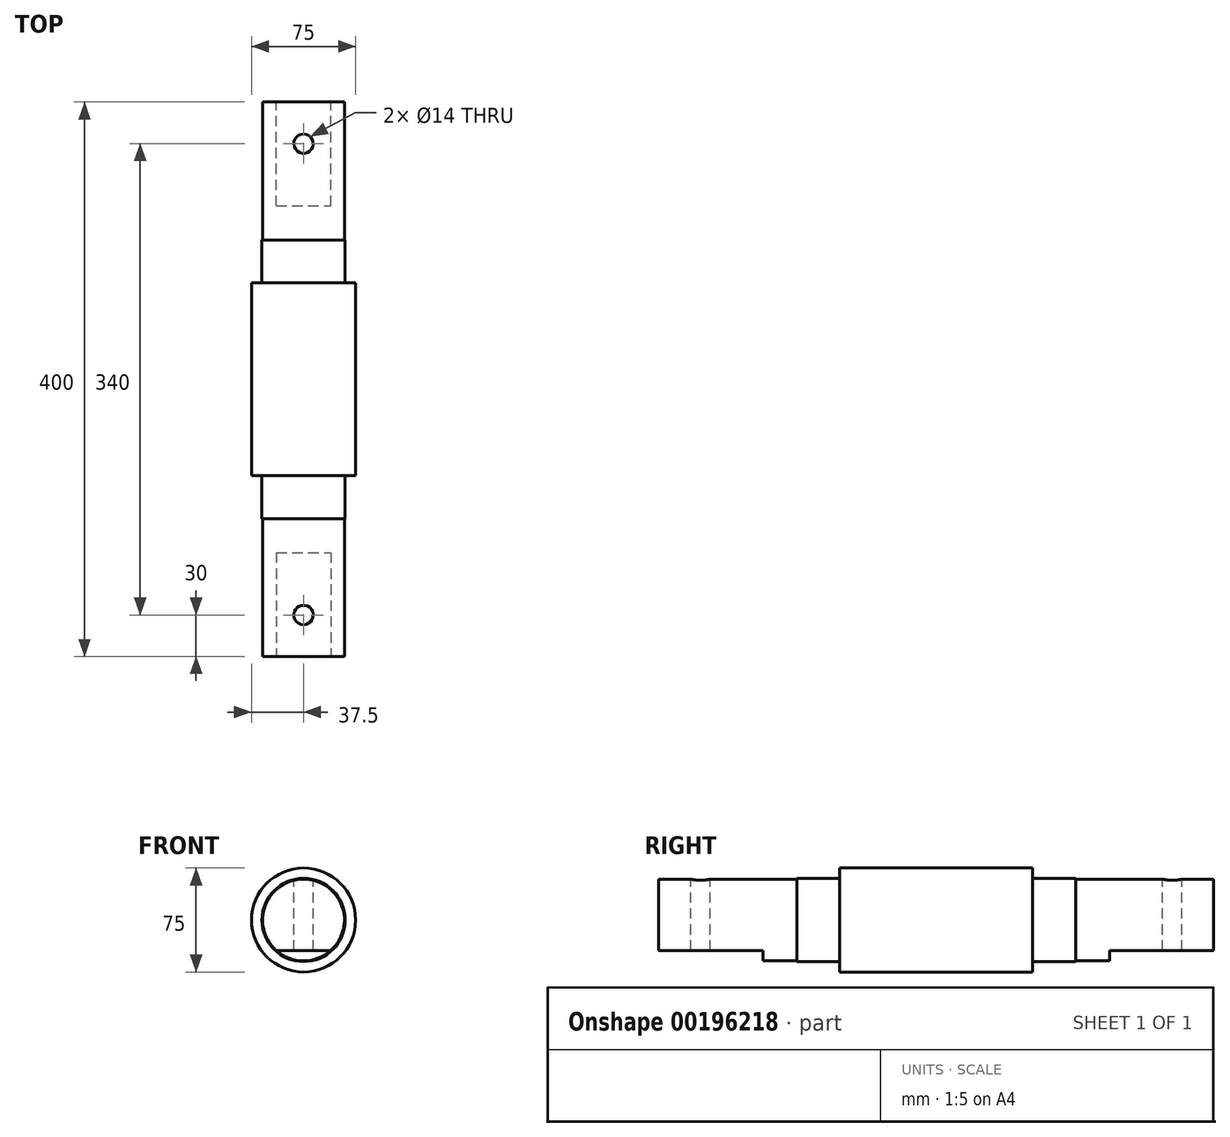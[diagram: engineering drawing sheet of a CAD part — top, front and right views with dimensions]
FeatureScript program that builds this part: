
annotation { "Feature Type Name" : "Feature", "Feature Type Description" : "" }
export const myFeature = defineFeature(function(context is Context, id is Id, definition is map)
    precondition{}
    {
        {
            var Q0;
            Q0=qCreatedBy(makeId("Front.planeOp"),FACE);
            var sketch = newSketch(context, id + "F0", { "sketchPlane" : qUnion([Q0])});
            skCircle(sketch, "E0", {"center": v(0, 0) * mm, "radius": 37.5 * mm});
            skSolve(sketch);
        }
        {
            var Q0;
            Q0 = qSketchRegion(id + "F0", true);
            extrude(context, id + "F1", {"entities" : qUnion([Q0]), "endBound" : BoundingType.SYMMETRIC, "oppositeDirection" : true, "depth" : 139 * mm});
        }
        {
            var Q0;
            Q0=makeQuery(id+"F1.opExtrude","CAP_FACE",FACE,{"disambiguationData":[OSD([sQuery(id+"F0.wireOp",EDGE,"E0")])],"isStart":true});
            var sketch = newSketch(context, id + "F2", { "sketchPlane" : qUnion([Q0])});
            skCircle(sketch, "E1", {"center": v(0, 0) * mm, "radius": 30 * mm});
            skSolve(sketch);
        }
        {
            var Q0;
            Q0 = qSketchRegion(id + "F2", true);
            extrude(context, id + "F3", {"entities" : qUnion([Q0]), "operationType" : NewBodyOperationType.ADD, "depth" : 31 * mm});
        }
        {
            var Q0;
            Q0=makeQuery(id+"F3.opExtrude","CAP_FACE",FACE,{"disambiguationData":[OSD([sQuery(id+"F2.wireOp",EDGE,"E1")])],"isStart":false});
            var sketch = newSketch(context, id + "F4", { "sketchPlane" : qUnion([Q0])});
            skCircle(sketch, "E2", {"center": v(0, 0) * mm, "radius": 29.5 * mm});
            skSolve(sketch);
        }
        {
            var Q0;
            Q0 = qSketchRegion(id + "F4", true);
            extrude(context, id + "F5", {"entities" : qUnion([Q0]), "operationType" : NewBodyOperationType.ADD, "depth" : 99.5 * mm});
        }
        {
            var Q0;
            Q0=makeQuery(id+"F5.opExtrude","CAP_FACE",FACE,{"disambiguationData":[OSD([sQuery(id+"F4.wireOp",EDGE,"E2")])],"isStart":false});
            var sketch = newSketch(context, id + "F6", { "sketchPlane" : qUnion([Q0])});
            skLineSegment(sketch, "E3", {"start": v(-19.65, -22) * mm, "end": v(19.65, -22) * mm});
            skSolve(sketch);
        }
        {
            var Q0;
            {var subQ0=sQuery(id+"F6.wireOp",EDGE,"E3");Q0=makeQuery(id+"F6.imprint","IMPRINT",FACE,{"disambiguationData":[TD([[makeQuery(id+"F6.imprint","IMPRINT",EDGE,{"derivedFrom":subQ0}),-1.0]])]});}
            extrude(context, id + "F7", {"entities" : qUnion([Q0]), "operationType" : NewBodyOperationType.REMOVE, "oppositeDirection" : true, "depth" : 75 * mm});
        }
        {
            var Q0;
            Q0=makeQuery(id+"F5.opExtrude","CAP_EDGE",EDGE,{"disambiguationData":[OSD([sQuery(id+"F4.wireOp",EDGE,"E2")])],"isStart":false});
            cPoint(context, id + "F8", {"entities" : qUnion([Q0]), "parameter" : 0.5});
        }
        {
            var Q0;
            Q0=qCreatedBy(makeId("Top.planeOp"),FACE);
            var Q1;
            Q1 = qCreatedBy(id + "F8" ,VERTEX);
            cPlane(context, id + "F9", {"entities" : qUnion([Q0, Q1]), "cplaneType" : CPlaneType.PLANE_POINT, "offset" : 25 * mm, "width" : 150 * mm, "height" : 150 * mm});
        }
        {
            var Q0;
            Q0=qCreatedBy(id+"F9.planeOp",FACE);
            var sketch = newSketch(context, id + "F10", { "sketchPlane" : qUnion([Q0])});
            skCircle(sketch, "E4", {"center": v(0, -170) * mm, "radius": 7 * mm});
            skSolve(sketch);
        }
        {
            var Q0;
            Q0=makeQuery(id+"F10.imprint","IMPRINT",FACE,{"disambiguationData":[TD([[makeQuery(id+"F10.imprint","IMPRINT",EDGE,{"derivedFrom":sQuery(id+"F10.wireOp",EDGE,"E4")}),1.0]])]});
            extrude(context, id + "F11", {"entities" : qUnion([Q0]), "operationType" : NewBodyOperationType.REMOVE, "endBound" : BoundingType.THROUGH_ALL, "oppositeDirection" : true, "depth" : 25 * mm});
        }
        {
            var Q0;
            Q0=makeQuery(id+"F1.opExtrude","SWEPT_BODY",BODY,{"disambiguationData":[OSD([sQuery(id+"F0.wireOp",EDGE,"E0")])]});
            var Q1;
            Q1=qCreatedBy(makeId("Front.planeOp"),FACE);
            mirror(context, id + "F12", {"operationType" : NewBodyOperationType.ADD, "entities" : qUnion([Q0]), "mirrorPlane" : qUnion([Q1])});
        }
    });
